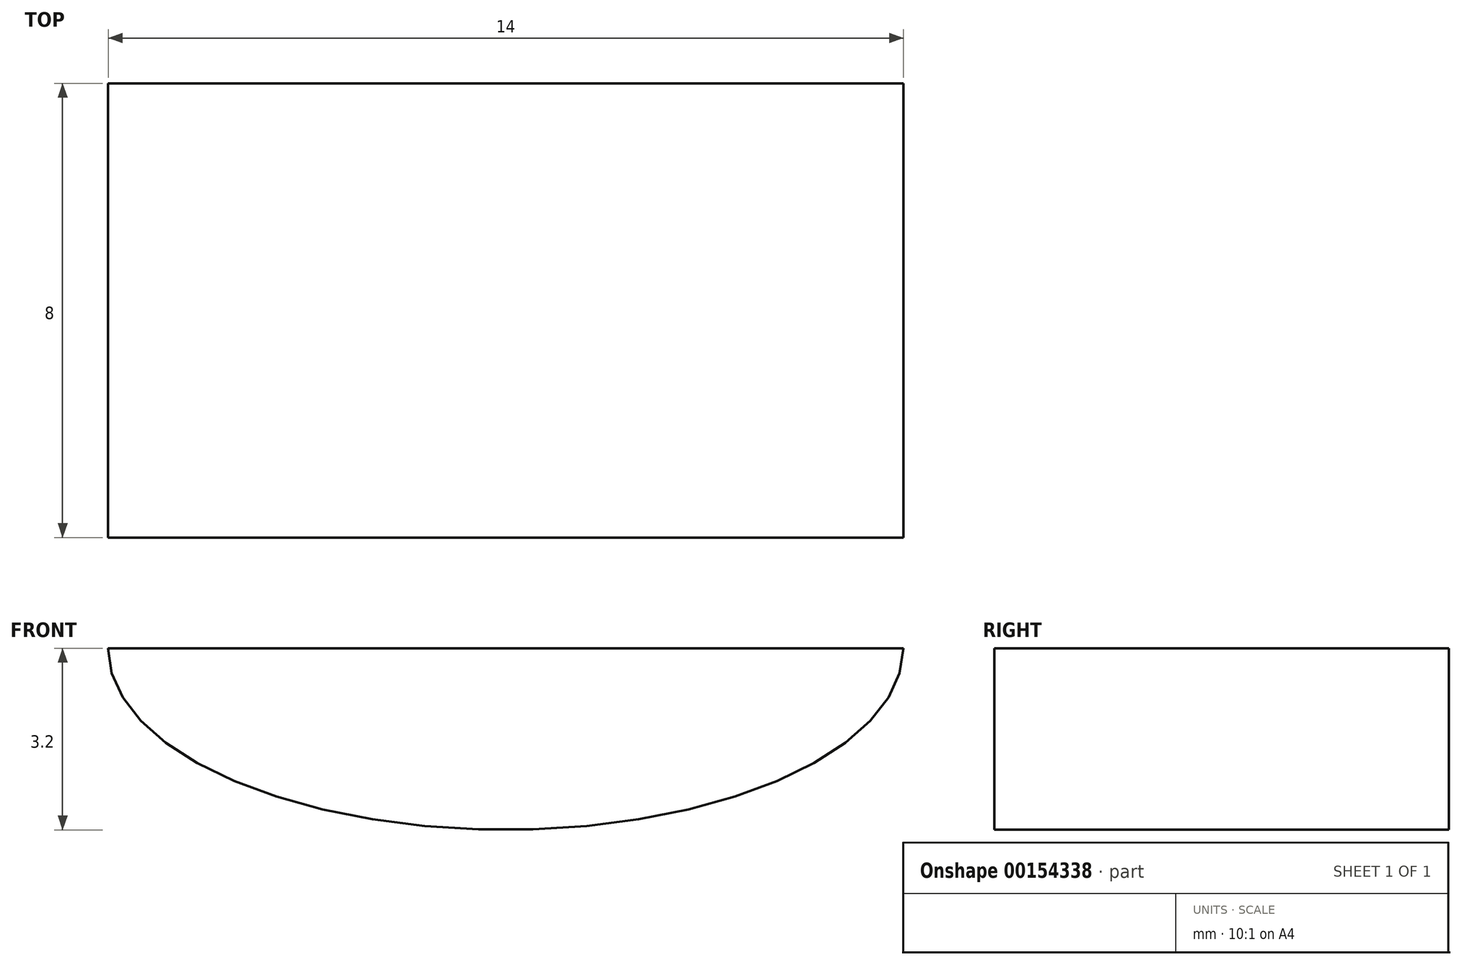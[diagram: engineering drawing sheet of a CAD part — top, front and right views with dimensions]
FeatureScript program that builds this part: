
annotation { "Feature Type Name" : "Feature", "Feature Type Description" : "" }
export const myFeature = defineFeature(function(context is Context, id is Id, definition is map)
    precondition{}
    {
        {
            var Q0;
            Q0=qCreatedBy(makeId("Front.planeOp"),FACE);
            var sketch = newSketch(context, id + "F0", { "sketchPlane" : qUnion([Q0])});
            skLineSegment(sketch, "E0", {"start": v(-62.72, 41.87) * mm, "end": v(-48.72, 41.87) * mm});
            skEllipticalArc(sketch, "E1", {});
            const initialGuessF0  = {"E1": [-0.05572391115128994, 0.04186743125319481, -1, 0, 0.007, 0.0031953981297186853, 0, 3.141592653589793]};
            skSetInitialGuess(sketch, initialGuessF0);
            skSolve(sketch);
        }
        {
            var Q0;
            Q0=makeQuery(id+"F0.imprint","IMPRINT",FACE,{"disambiguationData":[TD([[makeQuery(id+"F0.imprint","IMPRINT",EDGE,{"derivedFrom":sQuery(id+"F0.wireOp",EDGE,"E0")}),-1.0]])]});
            extrude(context, id + "F1", {"entities" : qUnion([Q0]), "depth" : 8 * mm});
        }
    });
